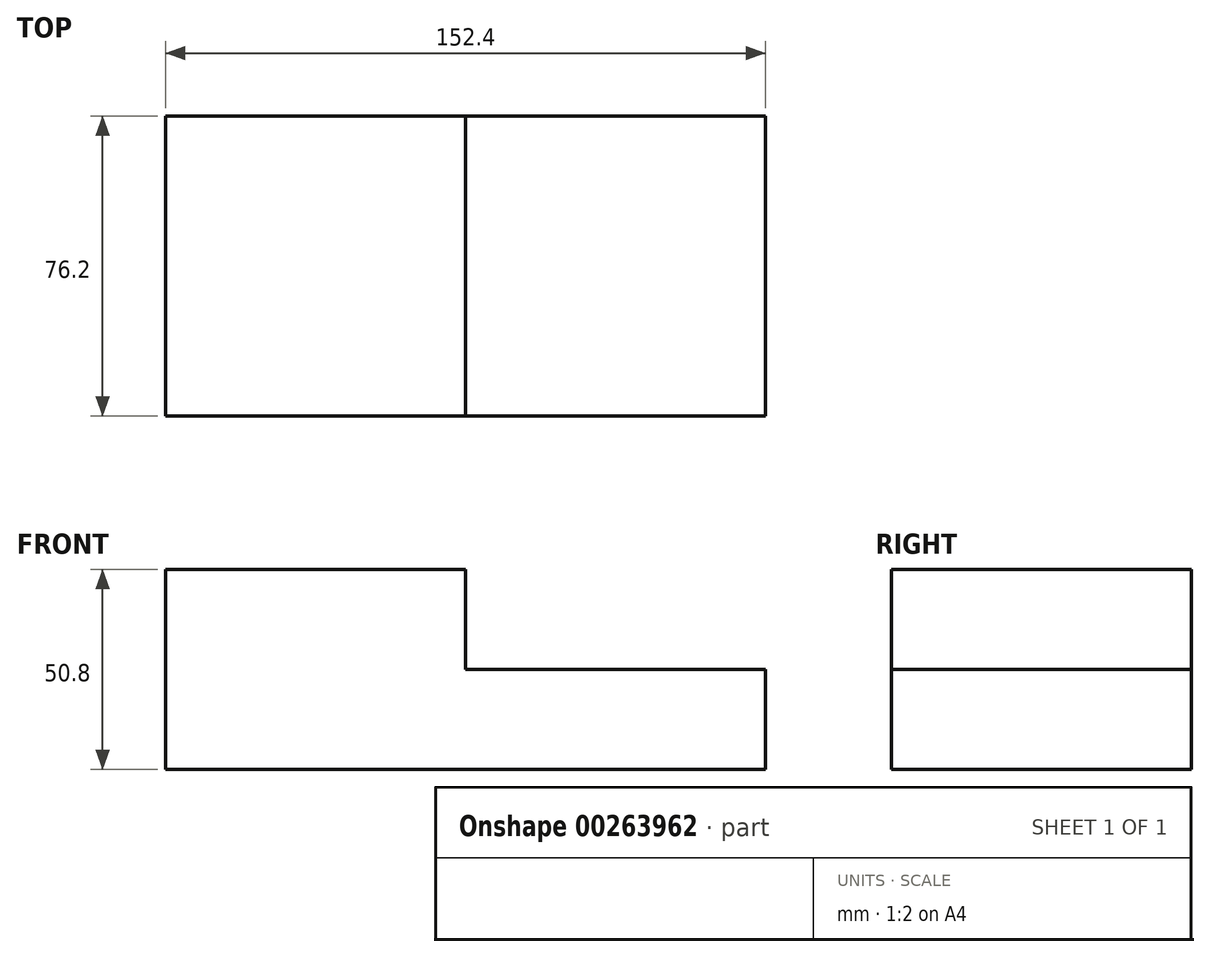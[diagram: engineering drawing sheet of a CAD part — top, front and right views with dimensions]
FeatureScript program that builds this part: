
annotation { "Feature Type Name" : "Feature", "Feature Type Description" : "" }
export const myFeature = defineFeature(function(context is Context, id is Id, definition is map)
    precondition{}
    {
        {
            var Q0;
            Q0=qCreatedBy(makeId("Front.planeOp"),FACE);
            var sketch = newSketch(context, id + "F0", { "sketchPlane" : qUnion([Q0])});
            skLineSegment(sketch, "E0.bottom", {"start": v(0, 0) * mm, "end": v(76.2, 0) * mm});
            skLineSegment(sketch, "E0.top", {"start": v(0, 50.8) * mm, "end": v(76.2, 50.8) * mm});
            skLineSegment(sketch, "E0.left", {"start": v(0, 0) * mm, "end": v(0, 50.8) * mm});
            skLineSegment(sketch, "E0.right", {"start": v(76.2, 0) * mm, "end": v(76.2, 50.8) * mm});
            skSolve(sketch);
        }
        {
            var Q0;
            Q0=makeQuery(id+"F0.imprint","IMPRINT",FACE,{"disambiguationData":[TD([[makeQuery(id+"F0.imprint","IMPRINT",EDGE,{"derivedFrom":sQuery(id+"F0.wireOp",EDGE,"E0.bottom")}),1.0]])]});
            extrude(context, id + "F1", {"entities" : qUnion([Q0]), "depth" : 76.2 * mm});
        }
        {
            var Q0;
            Q0=makeQuery(id+"F1.opExtrude","SWEPT_FACE",FACE,{"disambiguationData":[OSD([sQuery(id+"F0.wireOp",EDGE,"E0.right")])]});
            var sketch = newSketch(context, id + "F2", { "sketchPlane" : qUnion([Q0])});
            skLineSegment(sketch, "E1.bottom", {"start": v(0, 0) * mm, "end": v(-76.2, 0) * mm});
            skLineSegment(sketch, "E1.top", {"start": v(0, 25.4) * mm, "end": v(-76.2, 25.4) * mm});
            skLineSegment(sketch, "E1.left", {"start": v(0, 0) * mm, "end": v(0, 25.4) * mm});
            skLineSegment(sketch, "E1.right", {"start": v(-76.2, 0) * mm, "end": v(-76.2, 25.4) * mm});
            skSolve(sketch);
        }
        {
            var Q0;
            Q0=makeQuery(id+"F2.imprint","IMPRINT",FACE,{"disambiguationData":[TD([[makeQuery(id+"F2.imprint","IMPRINT",EDGE,{"derivedFrom":sQuery(id+"F2.wireOp",EDGE,"E1.bottom")}),1.0]])]});
            extrude(context, id + "F3", {"entities" : qUnion([Q0]), "operationType" : NewBodyOperationType.ADD, "depth" : 76.2 * mm});
        }
    });
